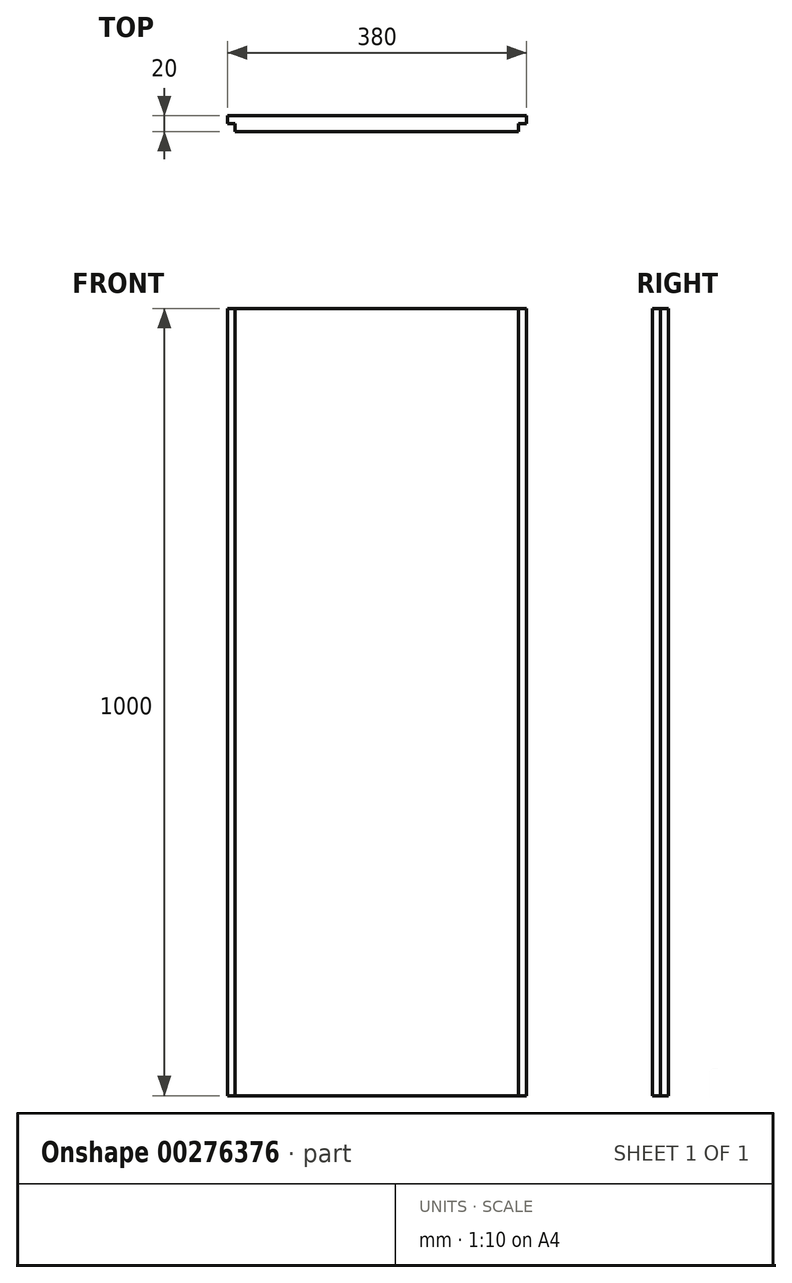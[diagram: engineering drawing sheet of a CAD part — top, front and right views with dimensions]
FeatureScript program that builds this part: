
annotation { "Feature Type Name" : "Feature", "Feature Type Description" : "" }
export const myFeature = defineFeature(function(context is Context, id is Id, definition is map)
    precondition{}
    {
        {
            var Q0;
            Q0=qCreatedBy(makeId("Front.planeOp"),FACE);
            var sketch = newSketch(context, id + "F0", { "sketchPlane" : qUnion([Q0])});
            skLineSegment(sketch, "E0.bottom", {"start": v(-210.56, 780.02) * mm, "end": v(169.44, 780.02) * mm});
            skLineSegment(sketch, "E0.top", {"start": v(-210.56, -219.98) * mm, "end": v(169.44, -219.98) * mm});
            skLineSegment(sketch, "E0.left", {"start": v(-210.56, 780.02) * mm, "end": v(-210.56, -219.98) * mm});
            skLineSegment(sketch, "E0.right", {"start": v(169.44, 780.02) * mm, "end": v(169.44, -219.98) * mm});
            skLineSegment(sketch, "E1", {"start": v(-200.56, 780.02) * mm, "end": v(-200.56, -219.98) * mm});
            skLineSegment(sketch, "E2", {"start": v(159.44, 780.02) * mm, "end": v(159.44, -219.98) * mm});
            skSolve(sketch);
        }
        {
            var Q0;
            {var subQ0=sQuery(id+"F0.wireOp",EDGE,"E1");Q0=makeQuery(id+"F0.imprint","IMPRINT",FACE,{"disambiguationData":[TD([[makeQuery(id+"F0.imprint","IMPRINT",EDGE,{"derivedFrom":subQ0}),1.0]])]});}
            extrude(context, id + "F1", {"entities" : qUnion([Q0]), "depth" : 20 * mm});
        }
        {
            var Q0;
            {var subQ0=sQuery(id+"F0.wireOp",EDGE,"E0.right");Q0=makeQuery(id+"F0.imprint","IMPRINT",FACE,{"disambiguationData":[TD([[makeQuery(id+"F0.imprint","IMPRINT",EDGE,{"derivedFrom":subQ0}),-1.0]])]});}
            var Q1;
            {var subQ0=sQuery(id+"F0.wireOp",EDGE,"E0.left");Q1=makeQuery(id+"F0.imprint","IMPRINT",FACE,{"disambiguationData":[TD([[makeQuery(id+"F0.imprint","IMPRINT",EDGE,{"derivedFrom":subQ0}),1.0]])]});}
            extrude(context, id + "F2", {"entities" : qUnion([Q0, Q1]), "operationType" : NewBodyOperationType.ADD, "depth" : 10 * mm});
        }
    });
